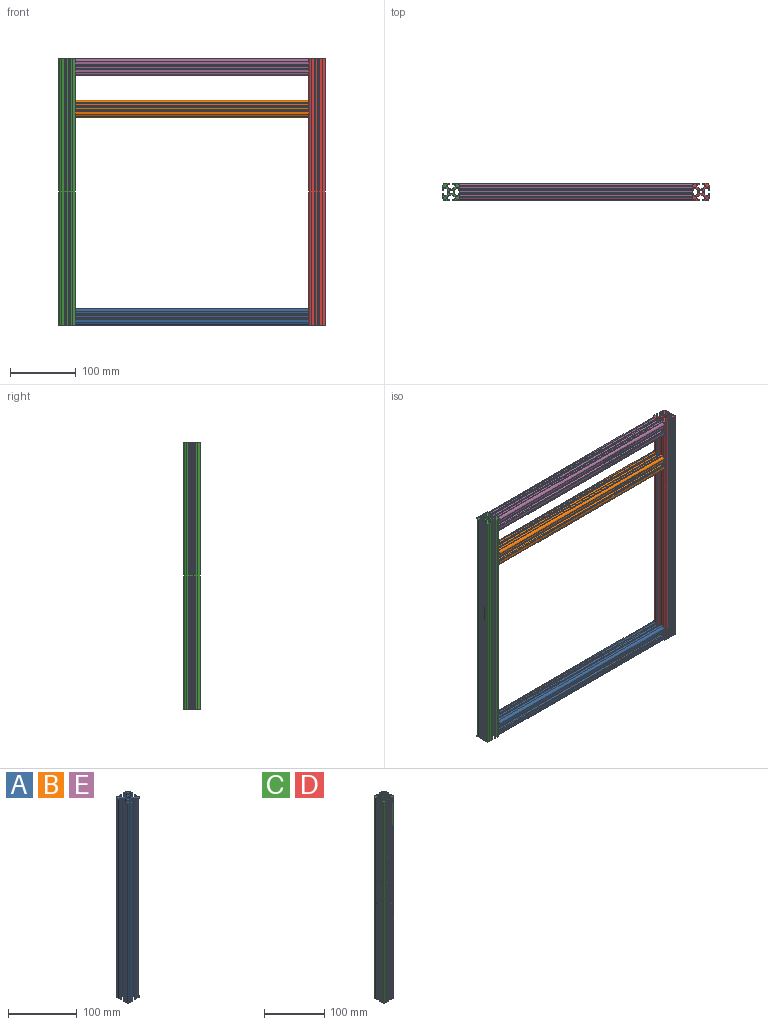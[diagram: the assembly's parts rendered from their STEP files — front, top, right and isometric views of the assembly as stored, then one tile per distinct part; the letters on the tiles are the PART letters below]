
ASSEMBLY  parts=5 mates=4
PART A: 81 faces, bbox 25.4x25.4x355.6 mm
  f0: cylinder r=0.77mm len=355.6mm, axis (0,0,-1), area 875.9mm2, adj f1,f77,f79,f80
  f1: plane 355.6x0.64mm, normal (0,1,0), area 226.9mm2, adj f0,f2,f79,f80
  f2: cylinder r=0.55mm len=355.6mm, axis (0,0,-1), area 607.5mm2, adj f1,f3,f79,f80
  f3: plane 355.6x3.14mm, normal (0,1,0), area 1115.7mm2, adj f2,f4,f79,f80
  f4: cylinder r=0.55mm len=355.6mm, axis (0,0,-1), area 615.8mm2, adj f3,f5,f79,f80
  f5: cylinder r=3.81mm len=355.6mm, axis (0,0,-1), area 2128.2mm2, adj f4,f6,f79,f80
  f6: plane 355.6x4.24mm, normal (-1,0,0), area 1507.8mm2, adj f5,f7,f79,f80
  f7: cylinder r=0.55mm len=355.6mm, axis (0,0,-1), area 617.5mm2, adj f6,f8,f79,f80
  f8: plane 355.6x0.64mm, normal (-1,0,0), area 227.6mm2, adj f7,f9,f79,f80
  f9: cylinder r=0.77mm len=355.6mm, axis (0,0,-1), area 851.7mm2, adj f8,f10,f79,f80
  f10: plane 355.6x1.73mm, normal (1,0,0), area 616.8mm2, adj f9,f11,f79,f80
  f11: cylinder r=1.91mm len=355.6mm, axis (0,0,-1), area 1596.1mm2, adj f10,f12,f79,f80
  f12: plane 355.6x1.85mm, normal (-0.71,-0.71,0), area 928.1mm2, adj f11,f13,f79,f80
  f13: cylinder r=3.81mm len=355.6mm, axis (0,0,-1), area 1064.1mm2, adj f12,f14,f79,f80
  f14: plane 355.6x2.91mm, normal (-1,0,0), area 1036.5mm2, adj f13,f15,f79,f80
  f15: cylinder r=3.81mm len=355.6mm, axis (0,0,-1), area 1064.1mm2, adj f14,f16,f79,f80
  f16: plane 355.6x1.85mm, normal (-0.71,0.71,0), area 928.1mm2, adj f15,f17,f79,f80
  f17: cylinder r=1.91mm len=355.6mm, axis (0,0,-1), area 1596.1mm2, adj f16,f18,f79,f80
  f18: plane 355.6x1.73mm, normal (1,0,0), area 616.8mm2, adj f17,f19,f79,f80
  f19: cylinder r=0.77mm len=355.6mm, axis (0,0,-1), area 864.3mm2, adj f18,f20,f79,f80
  f20: plane 355.6x0.64mm, normal (-1,0,0), area 225.9mm2, adj f19,f21,f79,f80
  f21: cylinder r=0.55mm len=355.6mm, axis (0,0,-1), area 580.1mm2, adj f20,f22,f79,f80
  f22: plane 355.6x3.15mm, normal (-1,0,0), area 1118.6mm2, adj f21,f23,f79,f80
  f23: cylinder r=0.55mm len=355.6mm, axis (0,0,-1), area 616mm2, adj f22,f24,f79,f80
  f24: cylinder r=3.81mm len=355.6mm, axis (0,0,-1), area 2128.2mm2, adj f23,f25,f79,f80
  f25: cylinder r=0.55mm len=355.6mm, axis (0,0,-1), area 617.6mm2, adj f24,f26,f79,f80
  f26: plane 355.6x3.78mm, normal (0,-1,0), area 1345.4mm2, adj f25,f27,f79,f80
  f27: cylinder r=0.55mm len=355.6mm, axis (0,0,-1), area 606mm2, adj f26,f28,f79,f80
  f28: cylinder r=0.77mm len=355.6mm, axis (0,0,-1), area 855.9mm2, adj f27,f29,f79,f80
  f29: plane 355.6x1.73mm, normal (0,1,0), area 616mm2, adj f28,f30,f79,f80
  f30: cylinder r=1.91mm len=355.6mm, axis (0,0,-1), area 1596.1mm2, adj f29,f31,f79,f80
  f31: plane 355.6x1.84mm, normal (0.71,-0.71,0), area 927mm2, adj f30,f32,f79,f80
  f32: cylinder r=3.81mm len=355.6mm, axis (0,0,-1), area 1064.1mm2, adj f31,f33,f79,f80
  f33: plane 355.6x2.91mm, normal (0,-1,0), area 1036.5mm2, adj f32,f34,f79,f80
  f34: cylinder r=3.81mm len=355.6mm, axis (0,0,-1), area 1064.1mm2, adj f33,f35,f79,f80
  f35: plane 355.6x1.84mm, normal (-0.71,-0.71,0), area 927mm2, adj f34,f36,f79,f80
  f36: cylinder r=1.91mm len=355.6mm, axis (0,0,-1), area 1596.1mm2, adj f35,f37,f79,f80
  f37: plane 355.6x1.73mm, normal (0,1,0), area 616mm2, adj f36,f38,f79,f80
  f38: cylinder r=0.79mm len=355.6mm, axis (0,0,-1), area 760.5mm2, adj f37,f39,f79,f80
  f39: plane 355.6x0.63mm, normal (0,-1,0), area 224.7mm2, adj f38,f40,f79,f80
  f40: cylinder r=0.55mm len=355.6mm, axis (0,0,-1), area 611.2mm2, adj f39,f41,f79,f80
  f41: plane 355.6x3.15mm, normal (0,-1,0), area 1121.4mm2, adj f40,f42,f79,f80
  f42: cylinder r=0.54mm len=355.6mm, axis (0,0,-1), area 608.2mm2, adj f41,f43,f79,f80
  f43: cylinder r=3.81mm len=355.6mm, axis (0,0,-1), area 2128.2mm2, adj f42,f44,f79,f80
  f44: cylinder r=0.55mm len=355.6mm, axis (0,0,-1), area 605.3mm2, adj f43,f45,f79,f80
  f45: plane 355.6x3.15mm, normal (1,0,0), area 1120.2mm2, adj f44,f46,f79,f80
  f46: cylinder r=0.55mm len=355.6mm, axis (0,0,-1), area 609.6mm2, adj f45,f47,f79,f80
  f47: plane 355.6x0.63mm, normal (1,0,0), area 225.3mm2, adj f46,f48,f79,f80
  f48: cylinder r=0.78mm len=355.6mm, axis (0,0,-1), area 827.4mm2, adj f47,f49,f79,f80
  f49: plane 355.6x1.73mm, normal (-1,0,0), area 616mm2, adj f48,f50,f79,f80
  f50: cylinder r=1.91mm len=355.6mm, axis (0,0,-1), area 1596.1mm2, adj f49,f51,f79,f80
  f51: plane 355.6x1.84mm, normal (0.71,0.71,0), area 927mm2, adj f50,f52,f79,f80
  f52: cylinder r=3.81mm len=355.6mm, axis (0,0,-1), area 1064.1mm2, adj f51,f53,f79,f80
  f53: plane 355.6x2.91mm, normal (1,0,0), area 1036.5mm2, adj f52,f54,f79,f80
  f54: cylinder r=3.81mm len=355.6mm, axis (0,0,-1), area 1064.1mm2, adj f53,f55,f79,f80
  f55: plane 355.6x1.84mm, normal (0.71,-0.71,0), area 927mm2, adj f54,f56,f79,f80
  f56: cylinder r=1.91mm len=355.6mm, axis (0,0,-1), area 1596.1mm2, adj f55,f57,f79,f80
  f57: plane 355.6x1.73mm, normal (-1,0,0), area 616mm2, adj f56,f58,f79,f80
  f58: cylinder r=0.78mm len=355.6mm, axis (0,0,-1), area 838.3mm2, adj f57,f59,f79,f80
  f59: plane 355.6x0.64mm, normal (1,0,0), area 227.6mm2, adj f58,f60,f79,f80
  f60: cylinder r=0.55mm len=355.6mm, axis (0,0,-1), area 610.1mm2, adj f59,f61,f79,f80
  f61: plane 355.6x3.15mm, normal (1,0,0), area 1119.2mm2, adj f60,f62,f79,f80
  f62: cylinder r=0.55mm len=355.6mm, axis (0,0,-1), area 614.1mm2, adj f61,f63,f79,f80
  f63: cylinder r=3.81mm len=355.6mm, axis (0,0,-1), area 2128.2mm2, adj f62,f64,f79,f80
  f64: cylinder r=0.56mm len=355.6mm, axis (0,0,-1), area 579.8mm2, adj f63,f65,f79,f80
  f65: plane 355.6x3.13mm, normal (0,1,0), area 1112.9mm2, adj f64,f66,f79,f80
  f66: cylinder r=0.55mm len=355.6mm, axis (0,0,-1), area 606.2mm2, adj f65,f67,f79,f80
  f67: plane 355.6x0.64mm, normal (0,1,0), area 228.3mm2, adj f66,f68,f79,f80
  f68: cylinder r=0.77mm len=355.6mm, axis (0,0,-1), area 890.6mm2, adj f67,f69,f79,f80
  f69: plane 355.6x1.73mm, normal (0,-1,0), area 616.8mm2, adj f68,f70,f79,f80
  f70: cylinder r=1.91mm len=355.6mm, axis (0,0,-1), area 1596.1mm2, adj f69,f71,f79,f80
  f71: plane 355.6x1.85mm, normal (-0.71,0.71,0), area 928.1mm2, adj f70,f72,f79,f80
  f72: cylinder r=3.81mm len=355.6mm, axis (0,0,-1), area 1064.1mm2, adj f71,f73,f79,f80
  f73: plane 355.6x2.91mm, normal (0,1,0), area 1036.5mm2, adj f72,f74,f79,f80
  f74: cylinder r=3.81mm len=355.6mm, axis (0,0,-1), area 1064.1mm2, adj f73,f75,f79,f80
  f75: plane 355.6x1.85mm, normal (0.71,0.71,0), area 928.1mm2, adj f74,f76,f79,f80
  f76: cylinder r=1.91mm len=355.6mm, axis (0,0,-1), area 1596.1mm2, adj f75,f77,f79,f80
  f77: plane 355.6x1.73mm, normal (0,-1,0), area 616.8mm2, adj f0,f76,f79,f80
  f78: cylinder r=3.36mm len=355.6mm, axis (0,0,-1), area 7512.8mm2, adj f79,f80
  f79: plane 25.4x25.4mm, normal (0,0,1), area 294.5mm2, adj f0,f1,f2,f3,f4,f5,f6,f7
  f80: plane 25.4x25.4mm, normal (0,0,-1), area 294.5mm2, adj f0,f1,f2,f3,f4,f5,f6,f7
PART B: same geometry as A
PART C: 81 faces, bbox 25.4x25.4x406.4 mm
  f0: cylinder r=0.77mm len=406.4mm, axis (0,0,-1), area 1001.1mm2, adj f1,f77,f79,f80
  f1: plane 406.4x0.64mm, normal (0,1,0), area 259.3mm2, adj f0,f2,f79,f80
  f2: cylinder r=0.55mm len=406.4mm, axis (0,0,-1), area 694.3mm2, adj f1,f3,f79,f80
  f3: plane 406.4x3.14mm, normal (0,1,0), area 1275.1mm2, adj f2,f4,f79,f80
  f4: cylinder r=0.55mm len=406.4mm, axis (0,0,-1), area 703.8mm2, adj f3,f5,f79,f80
  f5: cylinder r=3.81mm len=406.4mm, axis (0,0,-1), area 2432.2mm2, adj f4,f6,f79,f80
  f6: plane 406.4x4.24mm, normal (-1,0,0), area 1723.2mm2, adj f5,f7,f79,f80
  f7: cylinder r=0.55mm len=406.4mm, axis (0,0,-1), area 705.7mm2, adj f6,f8,f79,f80
  f8: plane 406.4x0.64mm, normal (-1,0,0), area 260.1mm2, adj f7,f9,f79,f80
  f9: cylinder r=0.77mm len=406.4mm, axis (0,0,-1), area 973.3mm2, adj f8,f10,f79,f80
  f10: plane 406.4x1.73mm, normal (1,0,0), area 704.9mm2, adj f9,f11,f79,f80
  f11: cylinder r=1.91mm len=406.4mm, axis (0,0,-1), area 1824.1mm2, adj f10,f12,f79,f80
  f12: plane 406.4x1.85mm, normal (-0.71,-0.71,0), area 1060.7mm2, adj f11,f13,f79,f80
  f13: cylinder r=3.81mm len=406.4mm, axis (0,0,-1), area 1216.1mm2, adj f12,f14,f79,f80
  f14: plane 406.4x2.91mm, normal (-1,0,0), area 1184.5mm2, adj f13,f15,f79,f80
  f15: cylinder r=3.81mm len=406.4mm, axis (0,0,-1), area 1216.1mm2, adj f14,f16,f79,f80
  f16: plane 406.4x1.85mm, normal (-0.71,0.71,0), area 1060.7mm2, adj f15,f17,f79,f80
  f17: cylinder r=1.91mm len=406.4mm, axis (0,0,-1), area 1824.1mm2, adj f16,f18,f79,f80
  f18: plane 406.4x1.73mm, normal (1,0,0), area 704.9mm2, adj f17,f19,f79,f80
  f19: cylinder r=0.77mm len=406.4mm, axis (0,0,-1), area 987.7mm2, adj f18,f20,f79,f80
  f20: plane 406.4x0.64mm, normal (-1,0,0), area 258.2mm2, adj f19,f21,f79,f80
  f21: cylinder r=0.55mm len=406.4mm, axis (0,0,-1), area 662.9mm2, adj f20,f22,f79,f80
  f22: plane 406.4x3.15mm, normal (-1,0,0), area 1278.4mm2, adj f21,f23,f79,f80
  f23: cylinder r=0.55mm len=406.4mm, axis (0,0,-1), area 704mm2, adj f22,f24,f79,f80
  f24: cylinder r=3.81mm len=406.4mm, axis (0,0,-1), area 2432.2mm2, adj f23,f25,f79,f80
  f25: cylinder r=0.55mm len=406.4mm, axis (0,0,-1), area 705.8mm2, adj f24,f26,f79,f80
  f26: plane 406.4x3.78mm, normal (0,-1,0), area 1537.6mm2, adj f25,f27,f79,f80
  f27: cylinder r=0.55mm len=406.4mm, axis (0,0,-1), area 692.5mm2, adj f26,f28,f79,f80
  f28: cylinder r=0.77mm len=406.4mm, axis (0,0,-1), area 978.2mm2, adj f27,f29,f79,f80
  f29: plane 406.4x1.73mm, normal (0,1,0), area 704mm2, adj f28,f30,f79,f80
  f30: cylinder r=1.91mm len=406.4mm, axis (0,0,-1), area 1824.1mm2, adj f29,f31,f79,f80
  f31: plane 406.4x1.84mm, normal (0.71,-0.71,0), area 1059.4mm2, adj f30,f32,f79,f80
  f32: cylinder r=3.81mm len=406.4mm, axis (0,0,-1), area 1216.1mm2, adj f31,f33,f79,f80
  f33: plane 406.4x2.91mm, normal (0,-1,0), area 1184.5mm2, adj f32,f34,f79,f80
  f34: cylinder r=3.81mm len=406.4mm, axis (0,0,-1), area 1216.1mm2, adj f33,f35,f79,f80
  f35: plane 406.4x1.84mm, normal (-0.71,-0.71,0), area 1059.4mm2, adj f34,f36,f79,f80
  f36: cylinder r=1.91mm len=406.4mm, axis (0,0,-1), area 1824.1mm2, adj f35,f37,f79,f80
  f37: plane 406.4x1.73mm, normal (0,1,0), area 704mm2, adj f36,f38,f79,f80
  f38: cylinder r=0.79mm len=406.4mm, axis (0,0,-1), area 869.2mm2, adj f37,f39,f79,f80
  f39: plane 406.4x0.63mm, normal (0,-1,0), area 256.7mm2, adj f38,f40,f79,f80
  f40: cylinder r=0.55mm len=406.4mm, axis (0,0,-1), area 698.5mm2, adj f39,f41,f79,f80
  f41: plane 406.4x3.15mm, normal (0,-1,0), area 1281.6mm2, adj f40,f42,f79,f80
  f42: cylinder r=0.54mm len=406.4mm, axis (0,0,-1), area 695.1mm2, adj f41,f43,f79,f80
  f43: cylinder r=3.81mm len=406.4mm, axis (0,0,-1), area 2432.2mm2, adj f42,f44,f79,f80
  f44: cylinder r=0.55mm len=406.4mm, axis (0,0,-1), area 691.8mm2, adj f43,f45,f79,f80
  f45: plane 406.4x3.15mm, normal (1,0,0), area 1280.2mm2, adj f44,f46,f79,f80
  f46: cylinder r=0.55mm len=406.4mm, axis (0,0,-1), area 696.7mm2, adj f45,f47,f79,f80
  f47: plane 406.4x0.63mm, normal (1,0,0), area 257.5mm2, adj f46,f48,f79,f80
  f48: cylinder r=0.78mm len=406.4mm, axis (0,0,-1), area 945.6mm2, adj f47,f49,f79,f80
  f49: plane 406.4x1.73mm, normal (-1,0,0), area 704mm2, adj f48,f50,f79,f80
  f50: cylinder r=1.91mm len=406.4mm, axis (0,0,-1), area 1824.1mm2, adj f49,f51,f79,f80
  f51: plane 406.4x1.84mm, normal (0.71,0.71,0), area 1059.4mm2, adj f50,f52,f79,f80
  f52: cylinder r=3.81mm len=406.4mm, axis (0,0,-1), area 1216.1mm2, adj f51,f53,f79,f80
  f53: plane 406.4x2.91mm, normal (1,0,0), area 1184.5mm2, adj f52,f54,f79,f80
  f54: cylinder r=3.81mm len=406.4mm, axis (0,0,-1), area 1216.1mm2, adj f53,f55,f79,f80
  f55: plane 406.4x1.84mm, normal (0.71,-0.71,0), area 1059.4mm2, adj f54,f56,f79,f80
  f56: cylinder r=1.91mm len=406.4mm, axis (0,0,-1), area 1824.1mm2, adj f55,f57,f79,f80
  f57: plane 406.4x1.73mm, normal (-1,0,0), area 704mm2, adj f56,f58,f79,f80
  f58: cylinder r=0.78mm len=406.4mm, axis (0,0,-1), area 958.1mm2, adj f57,f59,f79,f80
  f59: plane 406.4x0.64mm, normal (1,0,0), area 260.2mm2, adj f58,f60,f79,f80
  f60: cylinder r=0.55mm len=406.4mm, axis (0,0,-1), area 697.2mm2, adj f59,f61,f79,f80
  f61: plane 406.4x3.15mm, normal (1,0,0), area 1279.1mm2, adj f60,f62,f79,f80
  f62: cylinder r=0.55mm len=406.4mm, axis (0,0,-1), area 701.9mm2, adj f61,f63,f79,f80
  f63: cylinder r=3.81mm len=406.4mm, axis (0,0,-1), area 2432.2mm2, adj f62,f64,f79,f80
  f64: cylinder r=0.56mm len=406.4mm, axis (0,0,-1), area 662.6mm2, adj f63,f65,f79,f80
  f65: plane 406.4x3.13mm, normal (0,1,0), area 1271.8mm2, adj f64,f66,f79,f80
  f66: cylinder r=0.55mm len=406.4mm, axis (0,0,-1), area 692.8mm2, adj f65,f67,f79,f80
  f67: plane 406.4x0.64mm, normal (0,1,0), area 260.9mm2, adj f66,f68,f79,f80
  f68: cylinder r=0.77mm len=406.4mm, axis (0,0,-1), area 1017.9mm2, adj f67,f69,f79,f80
  f69: plane 406.4x1.73mm, normal (0,-1,0), area 704.9mm2, adj f68,f70,f79,f80
  f70: cylinder r=1.91mm len=406.4mm, axis (0,0,-1), area 1824.1mm2, adj f69,f71,f79,f80
  f71: plane 406.4x1.85mm, normal (-0.71,0.71,0), area 1060.7mm2, adj f70,f72,f79,f80
  f72: cylinder r=3.81mm len=406.4mm, axis (0,0,-1), area 1216.1mm2, adj f71,f73,f79,f80
  f73: plane 406.4x2.91mm, normal (0,1,0), area 1184.5mm2, adj f72,f74,f79,f80
  f74: cylinder r=3.81mm len=406.4mm, axis (0,0,-1), area 1216.1mm2, adj f73,f75,f79,f80
  f75: plane 406.4x1.85mm, normal (0.71,0.71,0), area 1060.7mm2, adj f74,f76,f79,f80
  f76: cylinder r=1.91mm len=406.4mm, axis (0,0,-1), area 1824.1mm2, adj f75,f77,f79,f80
  f77: plane 406.4x1.73mm, normal (0,-1,0), area 704.9mm2, adj f0,f76,f79,f80
  f78: cylinder r=3.36mm len=406.4mm, axis (0,0,-1), area 8586.1mm2, adj f79,f80
  f79: plane 25.4x25.4mm, normal (0,0,1), area 294.5mm2, adj f0,f1,f2,f3,f4,f5,f6,f7
  f80: plane 25.4x25.4mm, normal (0,0,-1), area 294.5mm2, adj f0,f1,f2,f3,f4,f5,f6,f7
PART D: same geometry as C
PART E: same geometry as A
PLACE A rot(axis=(0.71,0,-0.71),180deg) t=(134.53,53.26,-104.89)mm
PLACE B rot(axis=(-0.58,-0.58,0.58),120deg) t=(134.53,53.39,238.01)mm fixed
PLACE C t=(-221.07,27.86,-104.89)mm
PLACE D t=(159.93,27.86,-104.89)mm
PLACE E rot(axis=(0,-1,0),90deg) t=(134.53,27.86,301.51)mm
MATE fastened D.f22 <-> E.f80  axis (-1,0,0) through (134.53,35.91,301.51)mm
MATE fastened A.f79 <-> C.f61  axis (-1,0,0) through (-221.07,45.21,-104.89)mm
MATE fastened E.f79 <-> C.f45  axis (-1,0,0) through (-221.07,35.91,301.51)mm
MATE fastened B.f78 <-> C.f59  axis (-1,0,0) through (-221.07,40.69,225.31)mm
